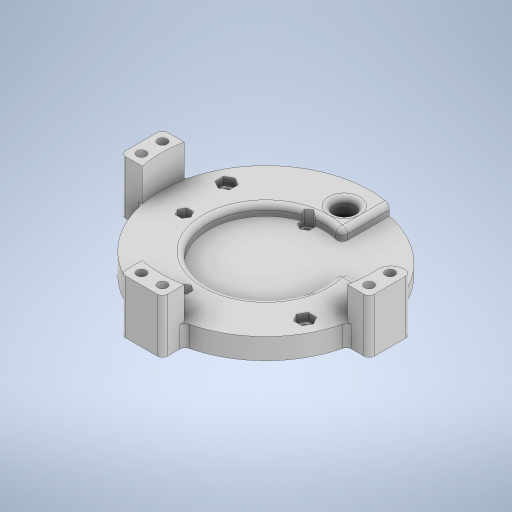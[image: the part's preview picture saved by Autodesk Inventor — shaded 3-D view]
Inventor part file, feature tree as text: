
AUTODESK INVENTOR PART (.ipt)
format: ipt  version: 2023 (Build 270158000, 158)  size: 592,384 bytes
history: native  units: in
note: dims shown in document units (in); Inventor stores cm internally (conversion verified against a paired STEP export)
features: sketch x17, extrude x13, fillet x8, hole x3
ambient origin geometry x8: Origin, YZ Plane, XZ Plane, XY Plane, X Axis, Y Axis, Z Axis, Center Point
bodies: Solid1 (feature_tree)
feature tree (41):
  extrude  "Extrusion1"  Depth=0.2in TaperAngle=0.0deg
  extrude  "Extrusion2"  Depth=0.2in TaperAngle=0.0deg
  extrude  "Extrusion3"  Depth=0.5in
  extrude  "Extrusion4"  Depth=0.4in
  fillet  "Fillet1"  Radius=0.5in
  fillet  "Fillet2"  Radius=0.5in
  fillet  "Fillet3"  Radius=0.4in
  extrude  "Extrusion5"  Depth=1.025in TaperAngle=0.0deg
  extrude  "Extrusion6"  Depth=0.2in
  extrude  "Extrusion8"  Depth=0.2in
  fillet  "Fillet4"  Radius=0.4in
  extrude  "Extrusion9"  Depth=0.2in
  sketch  "Sketch10"  dims[d26=0.4in d30=0.177in]
  hole  "Hole1"  [1 undecoded]
  extrude  "Extrusion10"  Depth=0.177in
  hole  "Hole2"  [1 undecoded]
  fillet  "Fillet5"  Radius=0.1in
  hole  "Hole3"  [1 undecoded]
  extrude  "Extrusion11"  Depth=0.625in TaperAngle=0.0deg
  fillet  "Fillet7"  Radius=0.3in
  extrude  "Extrusion13"  Depth=0.3in
  fillet  "Fillet8"  Radius=0.3in
  fillet  "Fillet9"  Radius=0.3in
  extrude  "Extrusion14"  Depth=0.1in
  extrude  "Extrusion15"  Depth=0.8875in
  sketch  "Sketch1"  dims[d0=4.0in d1=0.2in d2=0.0in]
  sketch  "Sketch2"  dims[d3=2.2in d4=0.2in d5=0.0in]
  sketch  "Sketch3"  dims[d6=3.75in d10=0.5in]
  sketch  "Sketch4"  dims[d11=0.4in d12=0.4in d13=0.5in d14=0.5in d15=0.4in]
  sketch  "Sketch5"  dims[d16=0.4in d17=1.025in d18=0.0in]
  sketch  "Sketch6"  dims[d19=0.2in d20=0.2in]
  sketch  "Sketch8"  dims[d21=0.4in d22=0.2in d23=0.4in]
  sketch  "Sketch9"  dims[d24=0.2in d25=0.2in]
  sketch  "Sketch11"  dims[d33=0.177in d34=0.177in]
  sketch  "Sketch12"  dims[d35=0.177in d36=5.0in d37=0.0in d38=0.1in]
  sketch  "Sketch13"  dims[d39=0.1in d40=0.1in]
  sketch  "Sketch14"  dims[d41=0.2in d42=0.0in d43=0.625in d44=0.0in d47=0.3in]
  sketch  "Sketch15"  dims[d48=0.3in d49=0.3in d50=0.3in d51=0.3in]
  sketch  "Sketch17"  dims[d52=0.2in d53=0.0in d54=0.1in]
  sketch  "Sketch18"  dims[d55=0.9in d56=0.8875in]
  sketch  "Sketch19"  dims[d57=0.8875in d58=0.25in d59=0.25in d60=0.2in d61=0.0in d62=0.126in d63=0.432in d64=0.256in d65=0.118in d66=90.0deg d67=0.5in d68=0.8108in d69=1.65in d70=45.0deg d71=1.65in d72=45.0deg d73=0.25in d74=0.2in d75=0.0in d76=0.126in d77=0.75in d78=0.375in d79=0.25in d80=0.5635in d81=1.0in d82=0.8108in d83=0.25in d84=0.4154in d85=0.2in d86=1.5in d87=0.75in d88=1.5in d89=0.75in d90=0.169in d91=0.75in d92=0.315in d93=0.157in d94=0.5635in d95=1.0in d96=0.8108in d97=0.6875in d98=0.0in d102=0.1in d103=1.5in d104=0.4in d105=1.0in d106=0.0in d107=0.1in d108=0.1in d109=0.28in d110=0.28in d111=0.22in d112=0.22in d113=0.22in d114=0.22in d115=0.15in d116=0.0in d117=0.15in d118=0.0in]
note: 3 required parameter values undecoded (feature->parameter linkage not recoverable at this tier; creation-order binding heuristic only, values carry confidence <= 0.55)
